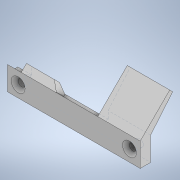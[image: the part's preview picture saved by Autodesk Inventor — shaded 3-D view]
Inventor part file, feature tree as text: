
AUTODESK INVENTOR PART (.ipt)
format: ipt  version: 2021 (Build 250183000, 183)  size: 166,400 bytes
history: native  units: mm
features: sketch x5, extrude x4, hole x1, chamfer x1
ambient origin geometry x8: Origin, YZ Plane, XZ Plane, XY Plane, X Axis, Y Axis, Z Axis, Center Point
bodies: Solid1 (feature_tree)
feature tree (11):
  extrude  "Extrusion1"  Depth=38.2mm
  hole  "Hole1"  [1 undecoded]
  extrude  "Extrusion2"  Depth=3.0mm
  extrude  "Extrusion3"  Depth=32.0mm
  extrude  "Extrusion4"  Depth=0.88mm
  chamfer  "Chamfer1"  Distance=12.0mm
  sketch  "Sketch1"  dims[d0=38.2mm d1=6.8mm]
  sketch  "Sketch2"  dims[d2=19.1mm d3=3.4mm]
  sketch  "Sketch3"  dims[d4=3.0mm d5=0.0mm d6=3.5mm]
  sketch  "Sketch4"  dims[d7=3.5mm d8=32.0mm]
  sketch  "Sketch5"  dims[d9=3.1mm d10=3.1mm d11=2.0mm d12=6.0mm d13=4.0mm d14=2.0mm d15=90.0deg d16=4.0mm d17=20.594885mm d18=12.0mm d19=45.0deg d20=1.2mm d21=38.2mm d22=0.0mm d23=4.0mm d24=4.0mm d25=14.0mm d26=26.0mm d27=3.0mm d28=0.0mm d29=0.88mm d30=0.0mm d31=2.0mm d32=2.0mm d33=45.0deg]
note: 1 required parameter value undecoded (feature->parameter linkage not recoverable at this tier; creation-order binding heuristic only, values carry confidence <= 0.55)
